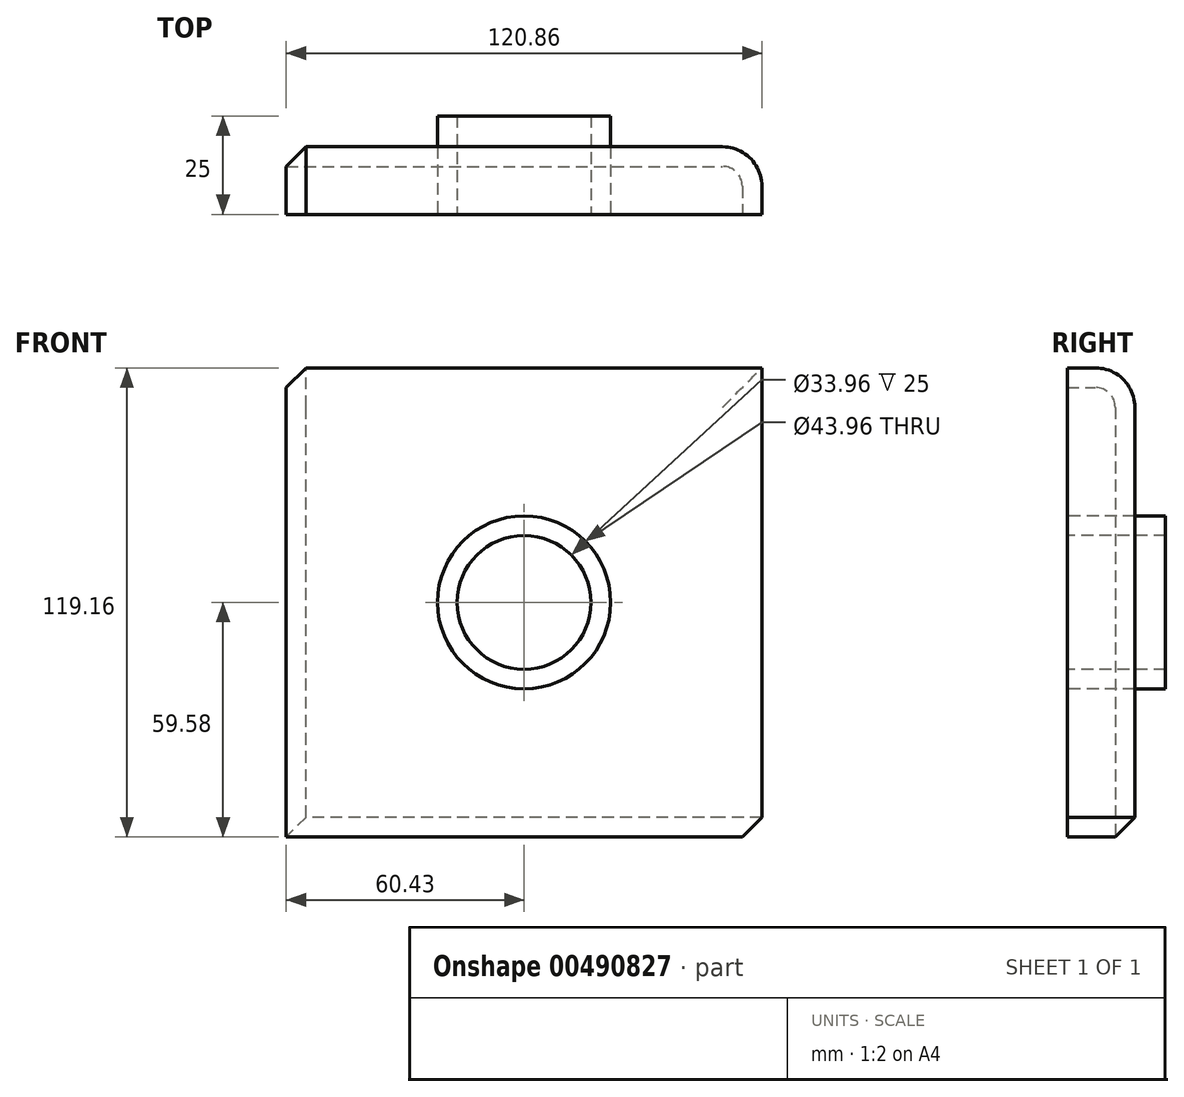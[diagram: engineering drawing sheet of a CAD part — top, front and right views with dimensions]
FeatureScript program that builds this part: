
annotation { "Feature Type Name" : "Feature", "Feature Type Description" : "" }
export const myFeature = defineFeature(function(context is Context, id is Id, definition is map)
    precondition{}
    {
        {
            var Q0;
            Q0=qCreatedBy(makeId("Front.planeOp"),FACE);
            var sketch = newSketch(context, id + "F0", { "sketchPlane" : qUnion([Q0])});
            skLineSegment(sketch, "E0.bottom", {"start": v(60.43, -59.58) * mm, "end": v(-60.43, -59.58) * mm});
            skLineSegment(sketch, "E0.top", {"start": v(60.43, 59.58) * mm, "end": v(-60.43, 59.58) * mm});
            skLineSegment(sketch, "E0.left", {"start": v(60.43, -59.58) * mm, "end": v(60.43, 59.58) * mm});
            skLineSegment(sketch, "E0.right", {"start": v(-60.43, -59.58) * mm, "end": v(-60.43, 59.58) * mm});
            skPoint(sketch, "E0.middle", {"position": v(0, 0) * mm});
            skCircle(sketch, "E1", {"center": v(0, 0) * mm, "radius": 21.98 * mm});
            skSolve(sketch);
        }
        {
            var Q0;
            Q0=makeQuery(id+"F0.imprint","IMPRINT",FACE,{"disambiguationData":[TD([[makeQuery(id+"F0.imprint","IMPRINT",EDGE,{"derivedFrom":sQuery(id+"F0.wireOp",EDGE,"E0.bottom")}),-1.0]])]});
            extrude(context, id + "F1", {"entities" : qUnion([Q0]), "oppositeDirection" : true, "depth" : 17.2 * mm});
        }
        {
            var Q0;
            Q0=qCreatedBy(makeId("Front.planeOp"),FACE);
            var sketch = newSketch(context, id + "F2", { "sketchPlane" : qUnion([Q0])});
            skCircle(sketch, "E2.0", {"center": v(0, 0) * mm, "radius": 21.98 * mm});
            skCircle(sketch, "E3.0", {"center": v(0, 0) * mm, "radius": 16.98 * mm});
            skSolve(sketch);
        }
        {
            var Q0;
            Q0 = qSketchRegion(id + "F2", true);
            extrude(context, id + "F3", {"entities" : qUnion([Q0]), "oppositeDirection" : true, "depth" : 25 * mm});
        }
        {
            var Q0;
            Q0=makeQuery(id+"F1.opExtrude","CAP_EDGE",EDGE,{"disambiguationData":[OSD([sQuery(id+"F0.wireOp",EDGE,"E0.top")])],"isStart":false});
            var Q1;
            Q1=makeQuery(id+"F1.opExtrude","CAP_EDGE",EDGE,{"disambiguationData":[OSD([sQuery(id+"F0.wireOp",EDGE,"E0.left")])],"isStart":false});
            fillet(context, id + "F4", {"entities" : qUnion([Q0, Q1]), "radius" : 10 * mm, "tangentPropagation" : true, "allowEdgeOverflow" : false});
        }
        {
            var Q0;
            Q0=makeQuery(id+"F1.opExtrude","CAP_EDGE",EDGE,{"disambiguationData":[OSD([sQuery(id+"F0.wireOp",EDGE,"E0.right")])],"isStart":false});
            var Q1;
            Q1=makeQuery(id+"F1.opExtrude","CAP_EDGE",EDGE,{"disambiguationData":[OSD([sQuery(id+"F0.wireOp",EDGE,"E0.bottom")])],"isStart":false});
            chamfer(context, id + "F5", {"entities" : qUnion([Q0, Q1]), "width" : 5 * mm, "tangentPropagation" : true});
        }
    });
